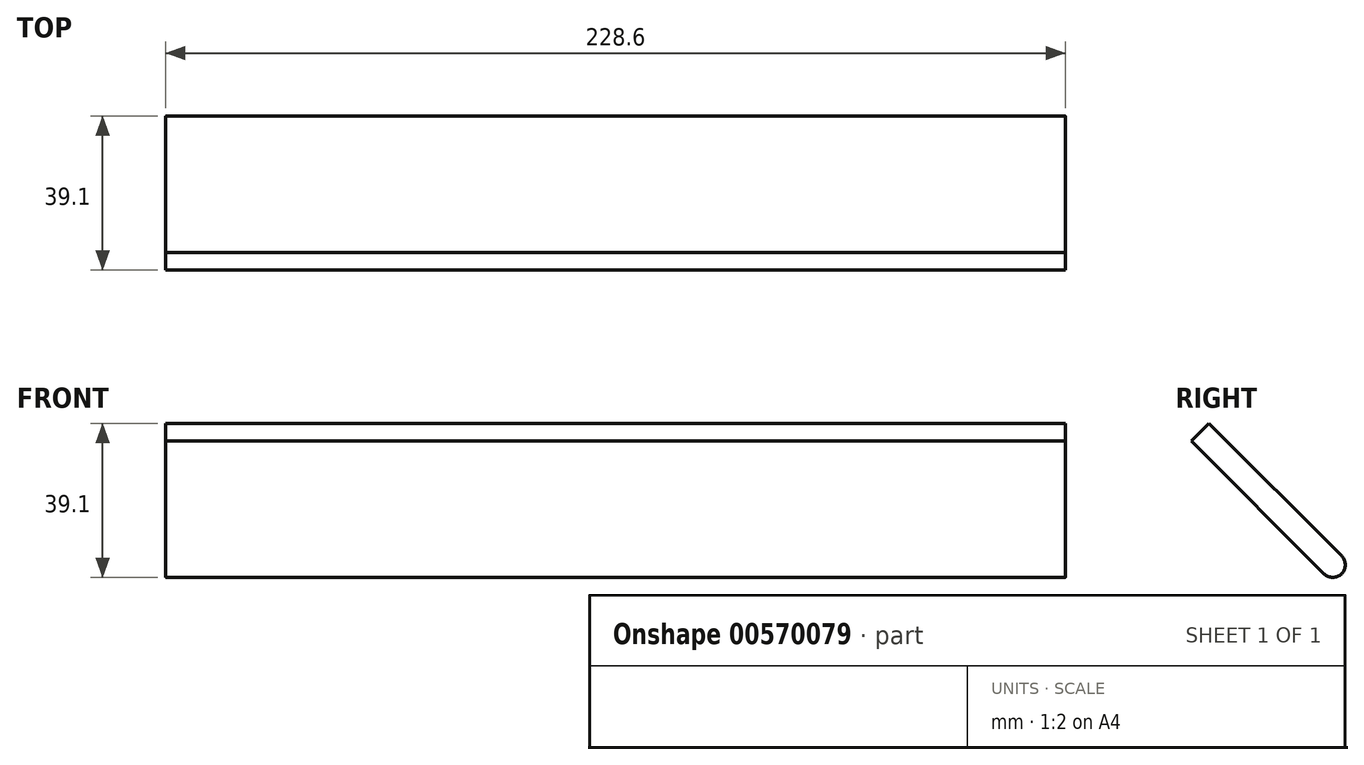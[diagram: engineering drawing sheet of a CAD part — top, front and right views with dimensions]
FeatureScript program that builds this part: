
annotation { "Feature Type Name" : "Feature", "Feature Type Description" : "" }
export const myFeature = defineFeature(function(context is Context, id is Id, definition is map)
    precondition{}
    {
        {
            var Q0;
            Q0=qCreatedBy(makeId("Right.planeOp"),FACE);
            var sketch = newSketch(context, id + "F0", { "sketchPlane" : qUnion([Q0])});
            skLineSegment(sketch, "E0", {"start": v(0, 0) * mm, "end": v(33.68, -33.68) * mm});
            skLineSegment(sketch, "E1", {"start": v(38.17, -33.68) * mm, "end": v(38.17, -33.68) * mm});
            skPoint(sketch, "E2.visualSharp", {"position": v(40.41, -31.43) * mm});
            skArc(sketch, "E2.filletArc", {"start": v(38.17, -33.68) * mm, "mid": v(39.1, -31.43) * mm, "end": v(38.17, -29.19) * mm});
            skPoint(sketch, "E3.visualSharp", {"position": v(35.92, -35.92) * mm});
            skArc(sketch, "E3.filletArc", {"start": v(33.68, -33.68) * mm, "mid": v(35.92, -34.6) * mm, "end": v(38.17, -33.68) * mm});
            skPoint(sketch, "E4.visualSharp", {"position": v(4.5, 4.5) * mm});
            skLineSegment(sketch, "E5", {"start": v(0, 0) * mm, "end": v(4.5, 4.5) * mm});
            skLineSegment(sketch, "E6", {"start": v(4.5, 4.5) * mm, "end": v(38.17, -29.19) * mm});
            skSolve(sketch);
        }
        {
            var Q0;
            Q0 = qSketchRegion(id + "F0", true);
            extrude(context, id + "F1", {"entities" : qUnion([Q0]), "oppositeDirection" : true, "depth" : 228.6 * mm, "offsetDistance" : 25.4 * mm});
        }
    });
